# Revit family: Air_Distribution-Fan_Coil_Units-ETI-CDV_CDVB_CDVM-v2
name_source: partatom
category: Mechanical Equipment
units: mm (PartAtom-declared; Revit-internal decimal feet)

## family parameters
Always vertical = No
Cut with Voids When Loaded = No
OmniClass Number = 23.75.70.17.27
OmniClass Title = Fan Coil Units
Part Type = Normal
Room Calculation Point = No
Round Connector Dimension = Use Radius
Shared = No
Work Plane-Based = Yes

## types (7) — shared parameters
Actual Chilled Water Flow = 0 GPM
Actual Condensate Drain Flow = 0 GPM
Actual Heating Water Flow = 0 GPM
Air Coil Fins per Inch = 12
Air Flow = 2157 CFM
Air Pressure Drop = 0.00 psi
Auxiliary Condensate Drain Connection Description = Auxiliary Drain
CTRL Service Box Visibility = Yes
CW Option 00 = Options_CW_Rows : 00
CW Option 03 = Options_CW_Rows : 03
CW Option 04 = Options_CW_Rows : 04
CW Option 06 = Options_CW_Rows : 06
Coil Pipe Material = Copper - JCI - Polished - Type-M
Condensate Drain Connection Diameter = 1"
Condensate Drain Connection Height = 19 3/4"
Condensate Drain Connection Radius = 0"
Configuration_LT = CDV_Config
Cooling Coil Air Pressure Drop = 0.26 psi
Cooling Coil Water Pressure Drop = 0.00 psi
Cooling Entering Dry Bulb Temperature = 75 °F
Cooling Entering Water Temperature = 0 °F
Cooling Entering Wet Bulb Temperature = 63 °F
Cooling Leaving Dry Bulb Temperature = 58 °F
Cooling Leaving Water Temperature = 0 °F
Cooling Leaving Wet Bulb Temperature = 55 °F
Default Elevation = 48"
Description = Vertical Fan-Coil Unit
Electric Heat Capacity = 0.0 Btu/h
Electric Heat Current = 0.0 A
Electric Heat Wattage = 0 W
External Static Pressure = 0.05 psi
Fan Motor HP = 0 kW
Fluid Velocity = 5 FPS
Frame Material = Metal - JCI - Steel - Galvanized - 18ga
Frequency = 60 Hz
Grille Material = Metal - JCI - Steel - Galvanized - Screen
HW Option 00 = Options_HW_Rows : 00
HW Option 01 = Options_HW_Rows : 01
HW Option 02 = Options_HW_Rows : 02
Has DX Cooling = No
Has Electric Heat = No
Heating Coil Air Pressure Drop = 0.12 psi
Heating Coil Water Pressure Drop = 6.02 psi
Heating Entering Dry Bulb Temperature = 70 °F
Heating Leaving Dry Bulb Temperature = 95 °F
Heating Water Entering Temperature = 180 °F
Heating Water Leaving Temperature = 160 °F
Hot Water Connection Diameter = 1"
Hot Water Connection Radius = 5/16"
Invalid Material = JCI - Area - Warning
Manufacturer = EnviroTec, Inc.
Minimum Air Flow = 0 CFM
Number of Poles = 1
Offset = 0"
Power Connector Description = Power Supply
Power Factor = 1
Product URL = https://www.enviro-tec.com
Product Video = https://www.youtube.com
Refrigerant Pressure Drop = 13.41 psi
Saturated Suction Temperature = 45 °F
Sensible Cooling Capacity = 40690.0 Btu/h
Sensible Heating Capacity = 57680.0 Btu/h
Shared Parameter File = JCI_Master_Shared_Parameters.txt
Superheat = 10 °F
Supply Air Connection Description = Supply Air Connection
Supply Coolant Temperature = 110 °F
Supply Fan Speed = High
Technical / Engineering Guide = FORM ET115.24-NOM8 (0521)
Total Cooling Capacity = 48860.0 Btu/h
URL = http://www.enviro-tec.com
Volt Option 277-PSC = Options_Voltage : 277-PSC
Voltage = 230 V
Warning Box Material = Warning
Zero = 0"
zero-valued in all types: Glycol Percentage

## per-type parameters (varying)
| type | Apparent Load | Coil Face Area | Discharge Grill Width | Discharge Grille Height | Fan Motor One Current | Fan Motor Quantity | Fan Quantity | Full Load Current | Length | Model | Model Number | Nominal Air Flow | Volt Option 115-ECM 3 SPD | Volt Option 115-PSC | Volt Option 208-ECM 3 SPD | Volt Option 208-PSC | Volt Option 230-ECM 3 SPD | Volt Option 230-PSC | Volt Option 277-ECM 3 SPD | Width |
| CDV_08 | 506 VA | 1.8 SF | 18" | 8" | 2.2 A | 1 | 1 | 2.2 A | 15" | CDV-08 | 8 | 800 CFM | Options_Voltage : 115-ECM 3 SPD | Options_Voltage : 115-PSC | Options_Voltage : 208-ECM 3 SPD | Options_Voltage : 208-PSC | Options_Voltage : 230-ECM 3 SPD | Options_Voltage : 230-PSC | Options_Voltage : 277-ECM 3 SPD | 22" |
| CDV_06 | 322 VA | 1.6 SF | 18" | 8" | 1.4 A | 1 | 1 | 1.4 A | 15" | CDV-06 | 6 | 600 CFM | Options_Voltage : 277-PSC | Options_Voltage : 277-PSC | Options_Voltage : 277-PSC | Options_Voltage : 277-PSC | Options_Voltage : 277-PSC | Options_Voltage : 277-PSC | Options_Voltage : 277-PSC | 22" |
| CDV_04 | 322 VA | 1.3 SF | 18" | 8" | 1.4 A | 1 | 1 | 1.4 A | 15" | CDV-04 | 4 | 400 CFM | Options_Voltage : 277-PSC | Options_Voltage : 277-PSC | Options_Voltage : 277-PSC | Options_Voltage : 277-PSC | Options_Voltage : 277-PSC | Options_Voltage : 277-PSC | Options_Voltage : 277-PSC | 22" |
| CDV_10 | 506 VA | 2.6 SF | 25" | 12" | 2.2 A | 1 | 1 | 2.2 A | 18" | CDV-10 | 10 | 1000 CFM | Options_Voltage : 277-PSC | Options_Voltage : 277-PSC | Options_Voltage : 277-PSC | Options_Voltage : 277-PSC | Options_Voltage : 277-PSC | Options_Voltage : 277-PSC | Options_Voltage : 277-PSC | 29" |
| CDV_12 | 920 VA | 2.9 SF | 25" | 12" | 4.0 A | 1 | 1 | 4.0 A | 18" | CDV-12 | 12 | 1200 CFM | Options_Voltage : 277-PSC | Options_Voltage : 277-PSC | Options_Voltage : 277-PSC | Options_Voltage : 277-PSC | Options_Voltage : 277-PSC | Options_Voltage : 277-PSC | Options_Voltage : 277-PSC | 29" |
| CDV_16 | 920 VA | 4 SF | 40" | 12" | 4.0 A | 2 | 2 | 4.0 A | 18" | CDV-16 | 16 | 1600 CFM | Options_Voltage : 277-PSC | Options_Voltage : 277-PSC | Options_Voltage : 277-PSC | Options_Voltage : 277-PSC | Options_Voltage : 277-PSC | Options_Voltage : 277-PSC | Options_Voltage : 277-PSC | 46" |
| CDV_20 | 920 VA | 5.1 SF | 40" | 12" | 4.0 A | 2 | 2 | 4.0 A | 18" | CDV-20 | 20 | 2000 CFM | Options_Voltage : 277-PSC | Options_Voltage : 277-PSC | Options_Voltage : 277-PSC | Options_Voltage : 277-PSC | Options_Voltage : 277-PSC | Options_Voltage : 277-PSC | Options_Voltage : 277-PSC | 46" |

## geometry (parser evidence)
native form markers: Blend x12, Revolve x4, Sweep x19
no freeform markers — native parametric forms only
